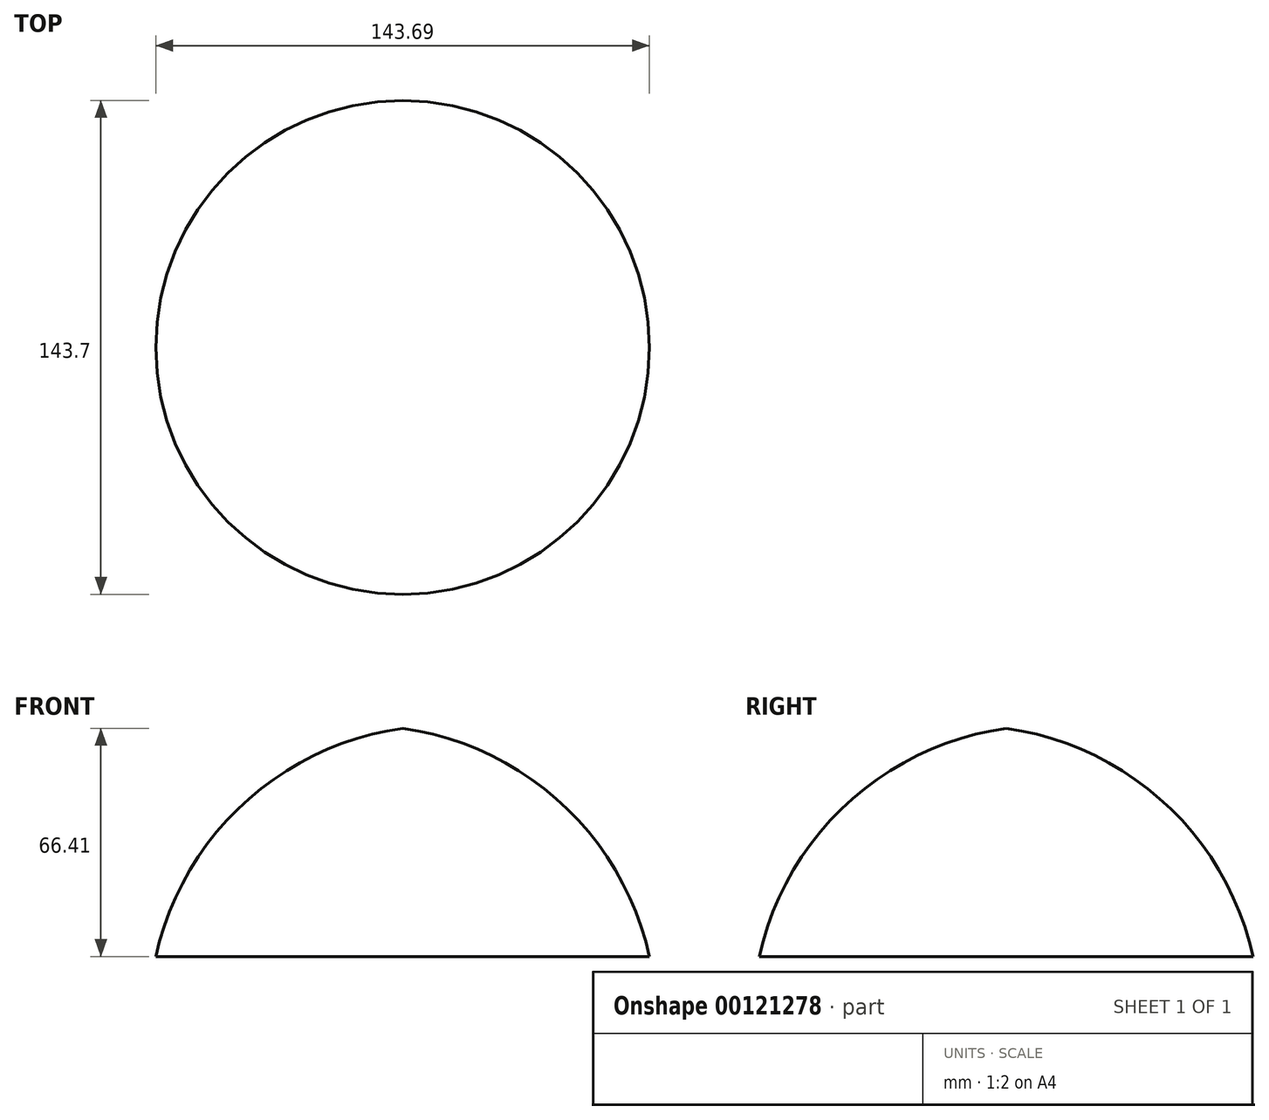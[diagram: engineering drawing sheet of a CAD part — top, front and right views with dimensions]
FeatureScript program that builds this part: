
annotation { "Feature Type Name" : "Feature", "Feature Type Description" : "" }
export const myFeature = defineFeature(function(context is Context, id is Id, definition is map)
    precondition{}
    {
        {
            var Q0;
            Q0=qCreatedBy(makeId("Front.planeOp"),FACE);
            var sketch = newSketch(context, id + "F0", { "sketchPlane" : qUnion([Q0])});
            skLineSegment(sketch, "E0", {"start": v(31.02, 38.92) * mm, "end": v(31.02, -27.49) * mm});
            skLineSegment(sketch, "E1", {"start": v(31.02, -27.49) * mm, "end": v(-40.82, -27.49) * mm});
            skArc(sketch, "E2", {"start": v(31.02, 38.92) * mm, "mid": v(-15.3, 16.97) * mm, "end": v(-40.82, -27.49) * mm});
            skSolve(sketch);
        }
        {
            var Q0;
            Q0 = qSketchRegion(id + "F0", true);
            var Q1;
            Q1=sQuery(id+"F0.wireOp",EDGE,"E0");
            revolve(context, id + "F1", {"entities" : qUnion([Q0]), "axis" : qUnion([Q1]), "revolveType" : RevolveType.FULL});
        }
    });
